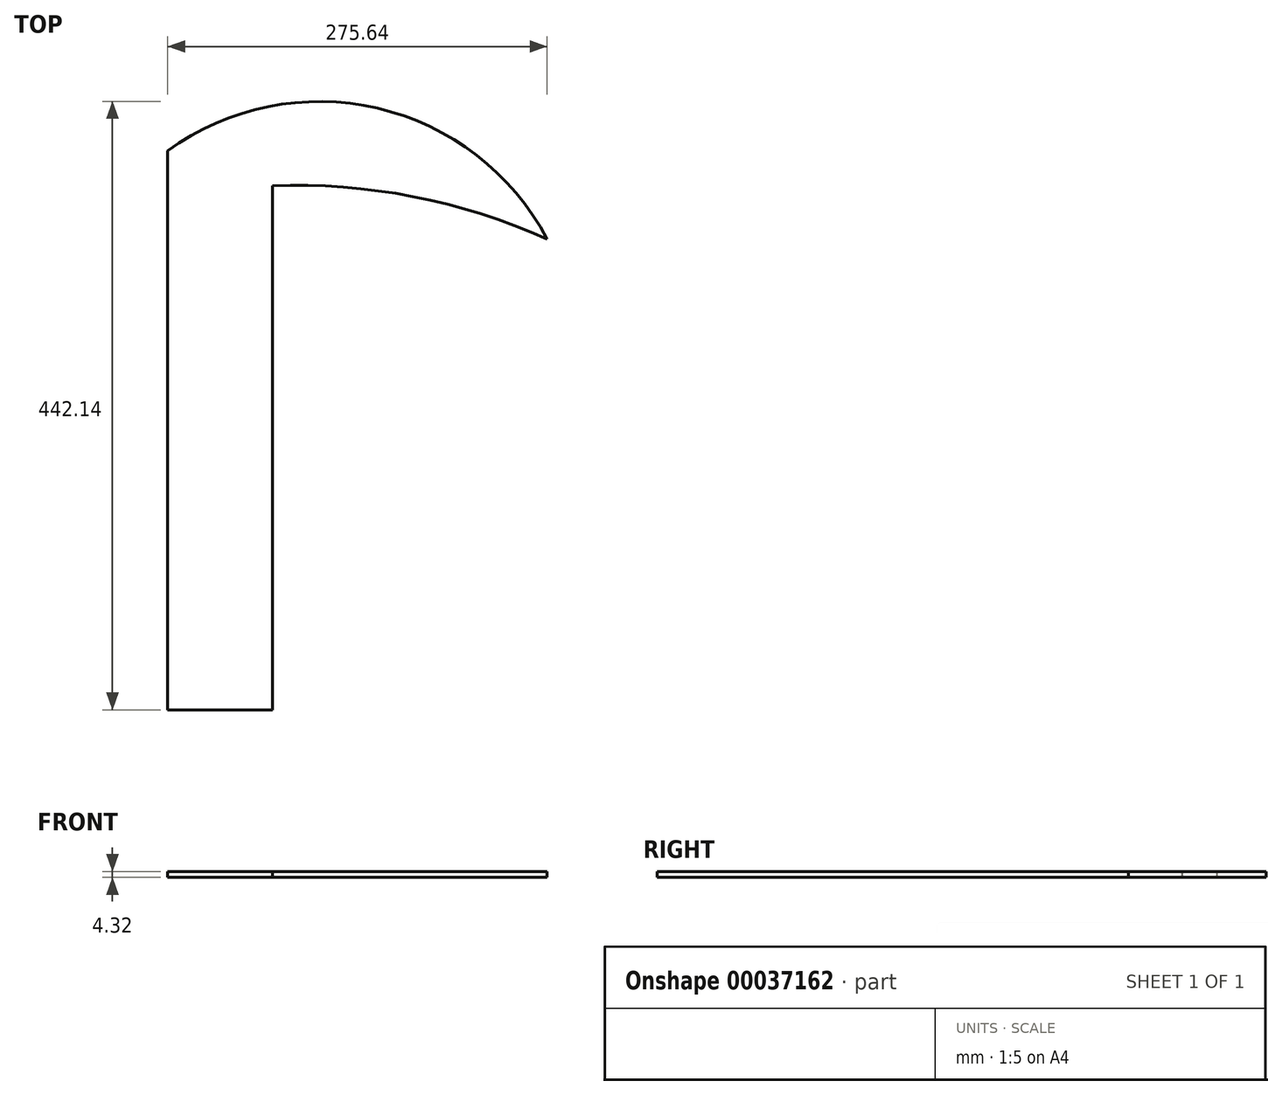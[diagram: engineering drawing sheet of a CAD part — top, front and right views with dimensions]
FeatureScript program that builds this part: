
annotation { "Feature Type Name" : "Feature", "Feature Type Description" : "" }
export const myFeature = defineFeature(function(context is Context, id is Id, definition is map)
    precondition{}
    {
        {
            var Q0;
            Q0=qCreatedBy(makeId("Top.planeOp"),FACE);
            var sketch = newSketch(context, id + "F0", { "sketchPlane" : qUnion([Q0])});
            skLineSegment(sketch, "E0", {"start": v(-60.85, -105.78) * mm, "end": v(15.35, -105.78) * mm});
            skLineSegment(sketch, "E1", {"start": v(15.35, -105.78) * mm, "end": v(15.35, 275.22) * mm});
            skLineSegment(sketch, "E2", {"start": v(-60.85, -105.78) * mm, "end": v(-60.85, 300.62) * mm});
            skArc(sketch, "E3", {"start": v(214.79, 236.5) * mm, "mid": v(91.6, 331.49) * mm, "end": v(-60.85, 300.62) * mm});
            skArc(sketch, "E4", {"start": v(214.79, 236.5) * mm, "mid": v(117.3, 267.3) * mm, "end": v(15.35, 275.22) * mm});
            skSolve(sketch);
        }
        {
            var Q0;
            Q0=makeQuery(id+"F0.imprint","IMPRINT",FACE,{"disambiguationData":[TD([[makeQuery(id+"F0.imprint","IMPRINT",EDGE,{"derivedFrom":sQuery(id+"F0.wireOp",EDGE,"E0")}),1.0]])]});
            extrude(context, id + "F1", {"entities" : qUnion([Q0]), "depth" : 4.32 * mm});
        }
    });
